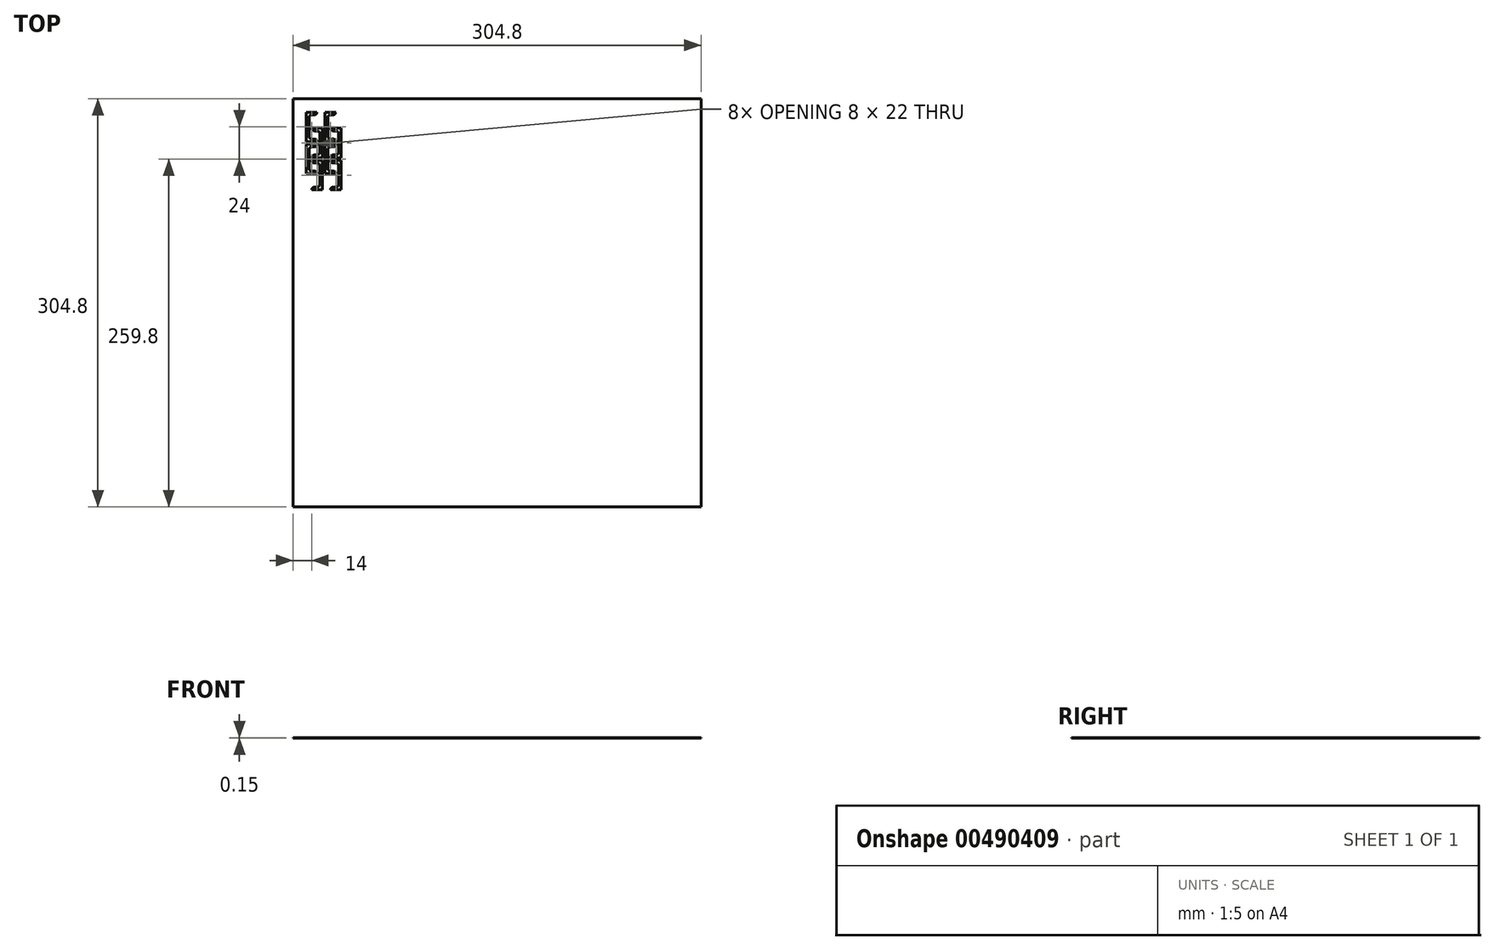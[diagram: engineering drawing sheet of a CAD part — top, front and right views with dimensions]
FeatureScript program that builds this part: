
annotation { "Feature Type Name" : "Feature", "Feature Type Description" : "" }
export const myFeature = defineFeature(function(context is Context, id is Id, definition is map)
    precondition{}
    {
        {
            var Q0;
            Q0=qCreatedBy(makeId("Top.planeOp"),FACE);
            var sketch = newSketch(context, id + "F0", { "sketchPlane" : qUnion([Q0])});
            skLineSegment(sketch, "E0.bottom", {"start": v(-152.4, 152.4) * mm, "end": v(152.4, 152.4) * mm});
            skLineSegment(sketch, "E0.top", {"start": v(-152.4, -152.4) * mm, "end": v(152.4, -152.4) * mm});
            skLineSegment(sketch, "E0.left", {"start": v(-152.4, 152.4) * mm, "end": v(-152.4, -152.4) * mm});
            skLineSegment(sketch, "E0.right", {"start": v(152.4, 152.4) * mm, "end": v(152.4, -152.4) * mm});
            skPoint(sketch, "E0.middle", {"position": v(0, 0) * mm});
            skLineSegment(sketch, "E1", {"start": v(-134.4, 142.4) * mm, "end": v(-142.4, 142.4) * mm});
            skLineSegment(sketch, "E2", {"start": v(-142.4, 142.4) * mm, "end": v(-142.4, 131.4) * mm});
            skLineSegment(sketch, "E3", {"start": v(-140.4, 131.4) * mm, "end": v(-140.4, 138.4) * mm});
            skLineSegment(sketch, "E4", {"start": v(-138.4, 140.4) * mm, "end": v(-136.4, 140.4) * mm});
            skArc(sketch, "E5.filletArc", {"start": v(-138.4, 140.4) * mm, "mid": v(-139.81, 139.81) * mm, "end": v(-140.4, 138.4) * mm});
            skArc(sketch, "E6.filletArc", {"start": v(-136.4, 140.4) * mm, "mid": v(-134.99, 140.99) * mm, "end": v(-134.4, 142.4) * mm});
            skLineSegment(sketch, "E7", {"start": v(-142.4, 131.4) * mm, "end": v(-140.4, 131.4) * mm, "construction": true});
            skLineSegment(sketch, "E8.MirrorCS", {"start": v(-140.4, 131.4) * mm, "end": v(-140.4, 124.4) * mm});
            skLineSegment(sketch, "E9.MirrorCS", {"start": v(-142.4, 120.4) * mm, "end": v(-142.4, 131.4) * mm});
            skLineSegment(sketch, "E10.MirrorCS", {"start": v(-138.4, 122.4) * mm, "end": v(-136.4, 122.4) * mm});
            skArc(sketch, "E11.MirrorCS", {"start": v(-138.4, 122.4) * mm, "mid": v(-139.81, 122.99) * mm, "end": v(-140.4, 124.4) * mm});
            skArc(sketch, "E12.MirrorCS", {"start": v(-136.4, 122.4) * mm, "mid": v(-134.99, 121.81) * mm, "end": v(-134.4, 120.4) * mm});
            skLineSegment(sketch, "E13.MirrorCS", {"start": v(-134.4, 120.4) * mm, "end": v(-142.4, 120.4) * mm});
            skLineSegment(sketch, "E14", {"start": v(-138.4, 108.4) * mm, "end": v(-130.4, 108.4) * mm});
            skLineSegment(sketch, "E15", {"start": v(-130.4, 108.4) * mm, "end": v(-130.4, 119.4) * mm});
            skLineSegment(sketch, "E16", {"start": v(-132.4, 119.4) * mm, "end": v(-132.4, 112.4) * mm});
            skLineSegment(sketch, "E17", {"start": v(-134.4, 110.4) * mm, "end": v(-136.4, 110.4) * mm});
            skArc(sketch, "E18.filletArc", {"start": v(-134.4, 110.4) * mm, "mid": v(-132.99, 110.99) * mm, "end": v(-132.4, 112.4) * mm});
            skArc(sketch, "E19.filletArc", {"start": v(-136.4, 110.4) * mm, "mid": v(-137.81, 109.81) * mm, "end": v(-138.4, 108.4) * mm});
            skLineSegment(sketch, "E20", {"start": v(-130.4, 119.4) * mm, "end": v(-132.4, 119.4) * mm, "construction": true});
            skLineSegment(sketch, "E21.MirrorCS", {"start": v(-132.4, 119.4) * mm, "end": v(-132.4, 126.4) * mm});
            skLineSegment(sketch, "E22.MirrorCS", {"start": v(-130.4, 130.4) * mm, "end": v(-130.4, 119.4) * mm});
            skLineSegment(sketch, "E23.MirrorCS", {"start": v(-134.4, 128.4) * mm, "end": v(-136.4, 128.4) * mm});
            skArc(sketch, "E24.MirrorCS", {"start": v(-134.4, 128.4) * mm, "mid": v(-132.99, 127.81) * mm, "end": v(-132.4, 126.4) * mm});
            skArc(sketch, "E25.MirrorCS", {"start": v(-136.4, 128.4) * mm, "mid": v(-137.81, 128.99) * mm, "end": v(-138.4, 130.4) * mm});
            skLineSegment(sketch, "E26.MirrorCS", {"start": v(-138.4, 130.4) * mm, "end": v(-130.4, 130.4) * mm});
            skLineSegment(sketch, "E27.0.1.0", {"start": v(-140.4, 107.4) * mm, "end": v(-140.4, 114.4) * mm});
            skLineSegment(sketch, "E27.0.1.1", {"start": v(-132.4, 95.4) * mm, "end": v(-132.4, 102.4) * mm});
            skLineSegment(sketch, "E27.0.1.2", {"start": v(-138.4, 106.4) * mm, "end": v(-130.4, 106.4) * mm});
            skLineSegment(sketch, "E27.0.1.3", {"start": v(-132.4, 95.4) * mm, "end": v(-132.4, 88.4) * mm});
            skLineSegment(sketch, "E27.0.1.4", {"start": v(-140.4, 107.4) * mm, "end": v(-140.4, 100.4) * mm});
            skLineSegment(sketch, "E27.0.1.5", {"start": v(-142.4, 96.4) * mm, "end": v(-142.4, 107.4) * mm});
            skLineSegment(sketch, "E27.0.1.6", {"start": v(-130.4, 106.4) * mm, "end": v(-130.4, 95.4) * mm});
            skLineSegment(sketch, "E27.0.1.7", {"start": v(-142.4, 118.4) * mm, "end": v(-142.4, 107.4) * mm});
            skLineSegment(sketch, "E27.0.1.8", {"start": v(-138.4, 84.4) * mm, "end": v(-130.4, 84.4) * mm});
            skLineSegment(sketch, "E27.0.1.9", {"start": v(-130.4, 84.4) * mm, "end": v(-130.4, 95.4) * mm});
            skLineSegment(sketch, "E27.0.1.10", {"start": v(-138.4, 98.4) * mm, "end": v(-136.4, 98.4) * mm});
            skArc(sketch, "E27.0.1.11", {"start": v(-136.4, 98.4) * mm, "mid": v(-134.99, 97.81) * mm, "end": v(-134.4, 96.4) * mm});
            skArc(sketch, "E27.0.1.12", {"start": v(-136.4, 104.4) * mm, "mid": v(-137.81, 104.99) * mm, "end": v(-138.4, 106.4) * mm});
            skArc(sketch, "E27.0.1.13", {"start": v(-134.4, 104.4) * mm, "mid": v(-132.99, 103.81) * mm, "end": v(-132.4, 102.4) * mm});
            skLineSegment(sketch, "E27.0.1.14", {"start": v(-134.4, 118.4) * mm, "end": v(-142.4, 118.4) * mm});
            skLineSegment(sketch, "E27.0.1.15", {"start": v(-134.4, 86.4) * mm, "end": v(-136.4, 86.4) * mm});
            skLineSegment(sketch, "E27.0.1.16", {"start": v(-134.4, 96.4) * mm, "end": v(-142.4, 96.4) * mm});
            skArc(sketch, "E27.0.1.17", {"start": v(-136.4, 116.4) * mm, "mid": v(-134.99, 116.99) * mm, "end": v(-134.4, 118.4) * mm});
            skArc(sketch, "E27.0.1.18", {"start": v(-138.4, 98.4) * mm, "mid": v(-139.81, 98.99) * mm, "end": v(-140.4, 100.4) * mm});
            skArc(sketch, "E27.0.1.19", {"start": v(-136.4, 86.4) * mm, "mid": v(-137.81, 85.81) * mm, "end": v(-138.4, 84.4) * mm});
            skLineSegment(sketch, "E27.0.1.20", {"start": v(-134.4, 104.4) * mm, "end": v(-136.4, 104.4) * mm});
            skLineSegment(sketch, "E27.0.1.21", {"start": v(-130.4, 95.4) * mm, "end": v(-132.4, 95.4) * mm, "construction": true});
            skArc(sketch, "E27.0.1.22", {"start": v(-134.4, 86.4) * mm, "mid": v(-132.99, 86.99) * mm, "end": v(-132.4, 88.4) * mm});
            skArc(sketch, "E27.0.1.23", {"start": v(-138.4, 116.4) * mm, "mid": v(-139.81, 115.81) * mm, "end": v(-140.4, 114.4) * mm});
            skLineSegment(sketch, "E27.0.1.24", {"start": v(-138.4, 116.4) * mm, "end": v(-136.4, 116.4) * mm});
            skLineSegment(sketch, "E27.0.1.25", {"start": v(-142.4, 107.4) * mm, "end": v(-140.4, 107.4) * mm, "construction": true});
            skLineSegment(sketch, "E27.1.0.0", {"start": v(-126.4, 131.4) * mm, "end": v(-126.4, 138.4) * mm});
            skLineSegment(sketch, "E27.1.0.1", {"start": v(-118.4, 119.4) * mm, "end": v(-118.4, 126.4) * mm});
            skLineSegment(sketch, "E27.1.0.2", {"start": v(-124.4, 130.4) * mm, "end": v(-116.4, 130.4) * mm});
            skLineSegment(sketch, "E27.1.0.3", {"start": v(-118.4, 119.4) * mm, "end": v(-118.4, 112.4) * mm});
            skLineSegment(sketch, "E27.1.0.4", {"start": v(-126.4, 131.4) * mm, "end": v(-126.4, 124.4) * mm});
            skLineSegment(sketch, "E27.1.0.5", {"start": v(-128.4, 120.4) * mm, "end": v(-128.4, 131.4) * mm});
            skLineSegment(sketch, "E27.1.0.6", {"start": v(-116.4, 130.4) * mm, "end": v(-116.4, 119.4) * mm});
            skLineSegment(sketch, "E27.1.0.7", {"start": v(-128.4, 142.4) * mm, "end": v(-128.4, 131.4) * mm});
            skLineSegment(sketch, "E27.1.0.8", {"start": v(-124.4, 108.4) * mm, "end": v(-116.4, 108.4) * mm});
            skLineSegment(sketch, "E27.1.0.9", {"start": v(-116.4, 108.4) * mm, "end": v(-116.4, 119.4) * mm});
            skLineSegment(sketch, "E27.1.0.10", {"start": v(-124.4, 122.4) * mm, "end": v(-122.4, 122.4) * mm});
            skArc(sketch, "E27.1.0.11", {"start": v(-122.4, 122.4) * mm, "mid": v(-120.99, 121.81) * mm, "end": v(-120.4, 120.4) * mm});
            skArc(sketch, "E27.1.0.12", {"start": v(-122.4, 128.4) * mm, "mid": v(-123.81, 128.99) * mm, "end": v(-124.4, 130.4) * mm});
            skArc(sketch, "E27.1.0.13", {"start": v(-120.4, 128.4) * mm, "mid": v(-118.99, 127.81) * mm, "end": v(-118.4, 126.4) * mm});
            skLineSegment(sketch, "E27.1.0.14", {"start": v(-120.4, 142.4) * mm, "end": v(-128.4, 142.4) * mm});
            skLineSegment(sketch, "E27.1.0.15", {"start": v(-120.4, 110.4) * mm, "end": v(-122.4, 110.4) * mm});
            skLineSegment(sketch, "E27.1.0.16", {"start": v(-120.4, 120.4) * mm, "end": v(-128.4, 120.4) * mm});
            skArc(sketch, "E27.1.0.17", {"start": v(-122.4, 140.4) * mm, "mid": v(-120.99, 140.99) * mm, "end": v(-120.4, 142.4) * mm});
            skArc(sketch, "E27.1.0.18", {"start": v(-124.4, 122.4) * mm, "mid": v(-125.81, 122.99) * mm, "end": v(-126.4, 124.4) * mm});
            skArc(sketch, "E27.1.0.19", {"start": v(-122.4, 110.4) * mm, "mid": v(-123.81, 109.81) * mm, "end": v(-124.4, 108.4) * mm});
            skLineSegment(sketch, "E27.1.0.20", {"start": v(-120.4, 128.4) * mm, "end": v(-122.4, 128.4) * mm});
            skLineSegment(sketch, "E27.1.0.21", {"start": v(-116.4, 119.4) * mm, "end": v(-118.4, 119.4) * mm, "construction": true});
            skArc(sketch, "E27.1.0.22", {"start": v(-120.4, 110.4) * mm, "mid": v(-118.99, 110.99) * mm, "end": v(-118.4, 112.4) * mm});
            skArc(sketch, "E27.1.0.23", {"start": v(-124.4, 140.4) * mm, "mid": v(-125.81, 139.81) * mm, "end": v(-126.4, 138.4) * mm});
            skLineSegment(sketch, "E27.1.0.24", {"start": v(-124.4, 140.4) * mm, "end": v(-122.4, 140.4) * mm});
            skLineSegment(sketch, "E27.1.0.25", {"start": v(-128.4, 131.4) * mm, "end": v(-126.4, 131.4) * mm, "construction": true});
            skLineSegment(sketch, "E27.1.1.0", {"start": v(-126.4, 107.4) * mm, "end": v(-126.4, 114.4) * mm});
            skLineSegment(sketch, "E27.1.1.1", {"start": v(-118.4, 95.4) * mm, "end": v(-118.4, 102.4) * mm});
            skLineSegment(sketch, "E27.1.1.2", {"start": v(-124.4, 106.4) * mm, "end": v(-116.4, 106.4) * mm});
            skLineSegment(sketch, "E27.1.1.3", {"start": v(-118.4, 95.4) * mm, "end": v(-118.4, 88.4) * mm});
            skLineSegment(sketch, "E27.1.1.4", {"start": v(-126.4, 107.4) * mm, "end": v(-126.4, 100.4) * mm});
            skLineSegment(sketch, "E27.1.1.5", {"start": v(-128.4, 96.4) * mm, "end": v(-128.4, 107.4) * mm});
            skLineSegment(sketch, "E27.1.1.6", {"start": v(-116.4, 106.4) * mm, "end": v(-116.4, 95.4) * mm});
            skLineSegment(sketch, "E27.1.1.7", {"start": v(-128.4, 118.4) * mm, "end": v(-128.4, 107.4) * mm});
            skLineSegment(sketch, "E27.1.1.8", {"start": v(-124.4, 84.4) * mm, "end": v(-116.4, 84.4) * mm});
            skLineSegment(sketch, "E27.1.1.9", {"start": v(-116.4, 84.4) * mm, "end": v(-116.4, 95.4) * mm});
            skLineSegment(sketch, "E27.1.1.10", {"start": v(-124.4, 98.4) * mm, "end": v(-122.4, 98.4) * mm});
            skArc(sketch, "E27.1.1.11", {"start": v(-122.4, 98.4) * mm, "mid": v(-120.99, 97.81) * mm, "end": v(-120.4, 96.4) * mm});
            skArc(sketch, "E27.1.1.12", {"start": v(-122.4, 104.4) * mm, "mid": v(-123.81, 104.99) * mm, "end": v(-124.4, 106.4) * mm});
            skArc(sketch, "E27.1.1.13", {"start": v(-120.4, 104.4) * mm, "mid": v(-118.99, 103.81) * mm, "end": v(-118.4, 102.4) * mm});
            skLineSegment(sketch, "E27.1.1.14", {"start": v(-120.4, 118.4) * mm, "end": v(-128.4, 118.4) * mm});
            skLineSegment(sketch, "E27.1.1.15", {"start": v(-120.4, 86.4) * mm, "end": v(-122.4, 86.4) * mm});
            skLineSegment(sketch, "E27.1.1.16", {"start": v(-120.4, 96.4) * mm, "end": v(-128.4, 96.4) * mm});
            skArc(sketch, "E27.1.1.17", {"start": v(-122.4, 116.4) * mm, "mid": v(-120.99, 116.99) * mm, "end": v(-120.4, 118.4) * mm});
            skArc(sketch, "E27.1.1.18", {"start": v(-124.4, 98.4) * mm, "mid": v(-125.81, 98.99) * mm, "end": v(-126.4, 100.4) * mm});
            skArc(sketch, "E27.1.1.19", {"start": v(-122.4, 86.4) * mm, "mid": v(-123.81, 85.81) * mm, "end": v(-124.4, 84.4) * mm});
            skLineSegment(sketch, "E27.1.1.20", {"start": v(-120.4, 104.4) * mm, "end": v(-122.4, 104.4) * mm});
            skLineSegment(sketch, "E27.1.1.21", {"start": v(-116.4, 95.4) * mm, "end": v(-118.4, 95.4) * mm, "construction": true});
            skArc(sketch, "E27.1.1.22", {"start": v(-120.4, 86.4) * mm, "mid": v(-118.99, 86.99) * mm, "end": v(-118.4, 88.4) * mm});
            skArc(sketch, "E27.1.1.23", {"start": v(-124.4, 116.4) * mm, "mid": v(-125.81, 115.81) * mm, "end": v(-126.4, 114.4) * mm});
            skLineSegment(sketch, "E27.1.1.24", {"start": v(-124.4, 116.4) * mm, "end": v(-122.4, 116.4) * mm});
            skLineSegment(sketch, "E27.1.1.25", {"start": v(-128.4, 107.4) * mm, "end": v(-126.4, 107.4) * mm, "construction": true});
            skLineSegment(sketch, "E27.direction1", {"start": v(-138.4, 108.4) * mm, "end": v(-124.4, 108.4) * mm, "construction": true});
            skLineSegment(sketch, "E27.direction2", {"start": v(-138.4, 108.4) * mm, "end": v(-138.4, 84.4) * mm, "construction": true});
            skSolve(sketch);
        }
        {
            var Q0;
            Q0=makeQuery(id+"F0.imprint","IMPRINT",FACE,{"disambiguationData":[TD([[makeQuery(id+"F0.imprint","IMPRINT",EDGE,{"derivedFrom":sQuery(id+"F0.wireOp",EDGE,"E0.bottom")}),-1.0]])]});
            extrude(context, id + "F1", {"entities" : qUnion([Q0]), "depth" : 0.15 * mm});
        }
    });
